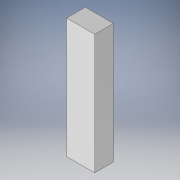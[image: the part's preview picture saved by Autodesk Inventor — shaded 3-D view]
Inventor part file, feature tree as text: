
AUTODESK INVENTOR PART (.ipt)
format: ipt  version: 2022.2 (Build 262287010, 287A)  size: 128,000 bytes
history: native  units: in
note: dims shown in document units (in); Inventor stores cm internally (conversion verified against a paired STEP export)
features: direct_edit x1, other x1, revolve x1
ambient origin geometry x8: Origin, YZ Plane, XZ Plane, XY Plane, X Axis, Y Axis, Z Axis, Center Point
bodies: Solid1 (feature_tree)
feature tree (3):
  direct_edit  "Direct Edit1"
  other  "Cap (5) (3)"
  revolve  "Rotate1"  [1 undecoded]
note: 1 required parameter value undecoded (feature->parameter linkage not recoverable at this tier; creation-order binding heuristic only, values carry confidence <= 0.55)
